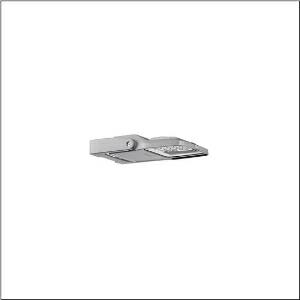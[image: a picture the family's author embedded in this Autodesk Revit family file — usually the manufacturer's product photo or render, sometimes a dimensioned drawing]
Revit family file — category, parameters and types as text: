
# Revit family: floodlight_fl_21_iq_micro___pl52_5xa7761a2d2a_1372
name_source: partatom
category: Lighting Fixtures
units: mm (PartAtom-declared; Revit-internal decimal feet)

## family parameters
Cut with Voids When Loaded = No
Host = Face
Light Source = No
Part Type = Normal
Room Calculation Point = No
Round Connector Dimension = Use Diameter
Shared = No

## types (1)
- --- (1 x LED, 2890 lm, 23.1 W, 3000K)
    Apparent Load = 23 VA
    CIE Flux Codes = 26 60 98 100 100
    Color Rendering = 70
    Color Temperature = 3000K
    Default Elevation = 1800 mm
    Description = Floodlight FL 21 iQ micro, floodlight, primary light control with lens, of PMMA, primary optical cover: protective disc, of toughened safety glass, transparent, light distribution: PL52, light emission: direct distribution, installation type: surface-mounted, lamps: LED, High Power LED, rated values: 2.890lm | 23,1W | 125,1lm/W (begin service life); end service life: 2.890lm | 23,8W; at 50% lumin. flux: 1.445lm | 11W | 131,4lm/W, colour temperature: 3000K, colour rendering: CRI > 70, light colour: 730, light setting 1 begin service life: 100% | 2.890lm | 23,1W | 125,1lm/W | 3.000K, light setting 1 end service life: 23,8W, further light settings possible, control: optimised constant luminous flux control (CLO 2.0), Desk-Remote (wireless, voltage-free reading and setting of iQ features in the workshop via application-optimized NFC function/RFID function), Light-Fading, Smart-Wire, Night-Set, Lumen-Switch, Temp-Guard, Auto-Match, pre-setting: linear dimming characteristic, with terminal, 6-pole, mains connection: 220..240V, AC, 50/60Hz, luminaire housing, of diecast aluminium, powder-coated, SITECO metallic grey (DB 702S), corrosivity category C5 mid according to DIN EN ISO 12944suitable for swimming poolschlorine-resistant, sealing non-destructively replaceable, design bracket, of diecast aluminium, powder-coated, SITECO metallic grey (DB 702S), protection rating (complete): IP66, insulation class (complete): insulation class II (safety insulation), certification: CE, ENEC, VDE, protection symbol: D, impact resistance: IK07, permissible operating ambient temperature: -40..+40°C, permissible operating ambient temperature for outdoor applications: -40..+50°C, standard: DIN EN 12944, LABS conformity tested according to VDMA 24364:2018-05, packaging unit: 1 piece

Light Distribution: PL52
    Height = 65 mm
    Lamp = 1 x LED
    Lamp Light Flux = 2890 lm
    Lamp Power = 23.1 W
    Lamp count = 1
    Length = 312 mm
    Luminous efficacy = 125 lm/W
    Manufacturer = Siteco
    ModVariant = No
    Model = 5XA7761A2D2A
    Mounting Place = Wall
    Mounting Type = Surface mounted
    Number of Poles = 1
    OnlyDefault = Yes
    Power Factor = 1
    Product Name = Floodlight FL 21 iQ micro | PL52
    Product group = floodlight | wall mounted
    ProductGroupID = 2002
    Protection Class = Protection class II
    Protection Degree = IP 66
    RLX_Detail_Level = 1
    RLX_Emergency_Light_Flux = 0 lm
    RLX_Emergency_Type = 0
    RLX_Emergency_Type_DB = No
    RlxData = <blob elided: 97969 chars, md5=2c1b814f>
    Socket = socket
    Standby Power = 0 W
    System Light Flux = 2890 lm
    System Power = 23 W
    Type Comments = factory setting: luminous flux: 100 % | dim-lin: 254 | 455 mA
    Type Image = l_1006878.jpg
    URL = http://relux.com
    VarID = @adj_177615
    Voltage = 0 V
    Weight = 0.00 kg
    Width = 230 mm

## geometry (parser evidence)
native form markers: Blend x4, Sweep x14
no freeform markers — native parametric forms only
